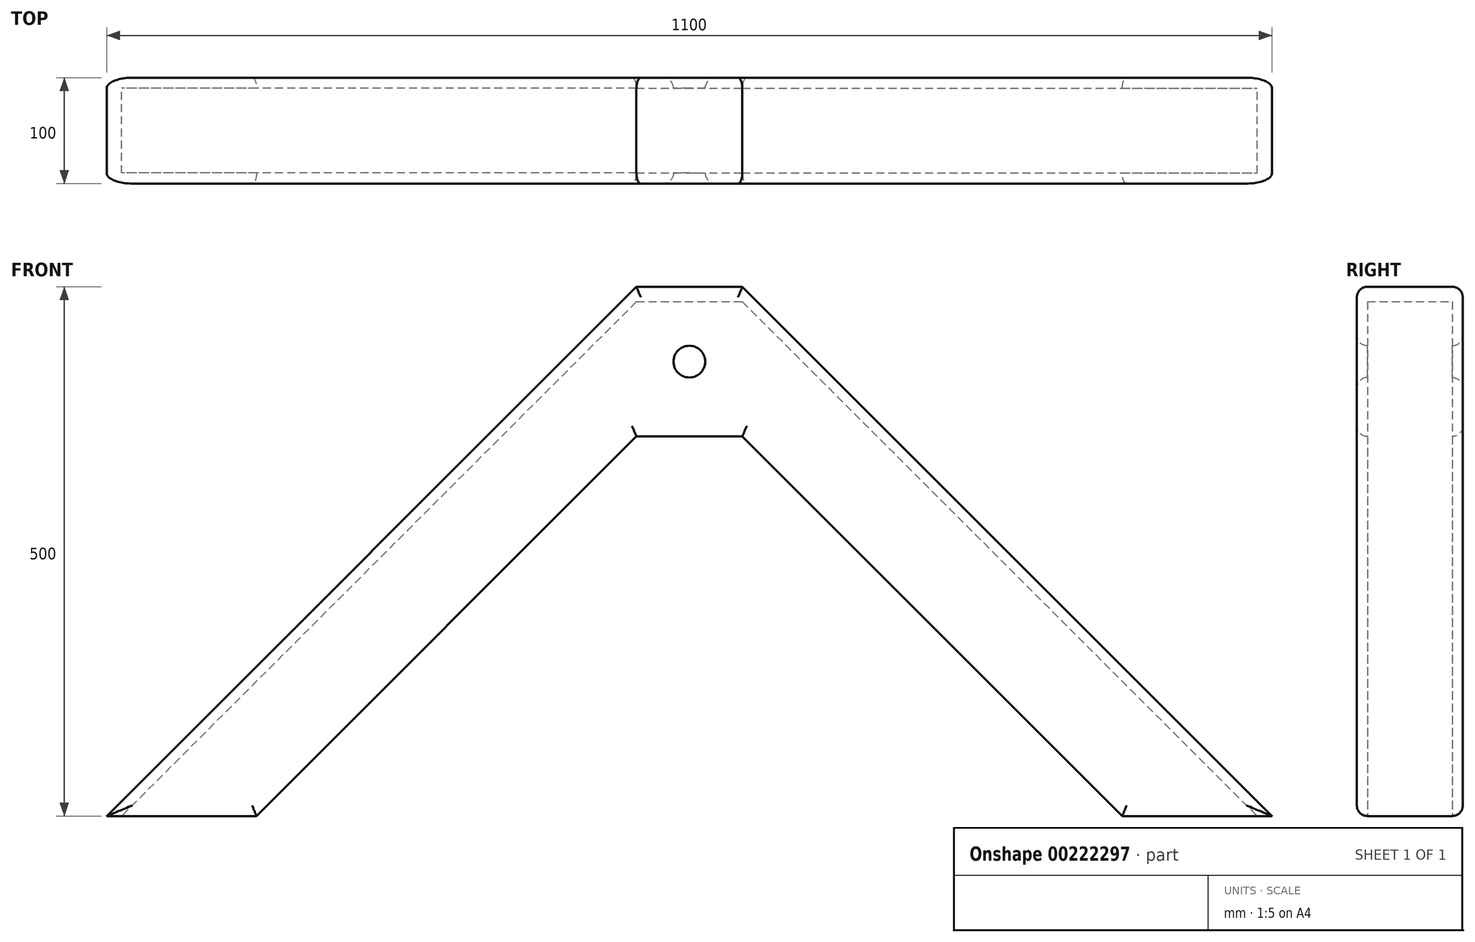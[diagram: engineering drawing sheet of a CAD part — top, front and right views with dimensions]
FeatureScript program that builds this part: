
annotation { "Feature Type Name" : "Feature", "Feature Type Description" : "" }
export const myFeature = defineFeature(function(context is Context, id is Id, definition is map)
    precondition{}
    {
        {
            var Q0;
            Q0=qCreatedBy(makeId("Front.planeOp"),FACE);
            var sketch = newSketch(context, id + "F0", { "sketchPlane" : qUnion([Q0])});
            skLineSegment(sketch, "E0", {"start": v(0, 500) * mm, "end": v(500, 0) * mm});
            skLineSegment(sketch, "E1.0", {"start": v(0, 358.58) * mm, "end": v(358.58, 0) * mm});
            skLineSegment(sketch, "E2", {"start": v(0, 500) * mm, "end": v(0, 0) * mm, "construction": true});
            skLineSegment(sketch, "E3", {"start": v(0, 0) * mm, "end": v(500, 0) * mm, "construction": true});
            skLineSegment(sketch, "E4", {"start": v(0, 485.86) * mm, "end": v(485.86, 0) * mm});
            skLineSegment(sketch, "E5", {"start": v(208.02, 291.98) * mm, "end": v(200.95, 284.9) * mm, "construction": true});
            skLineSegment(sketch, "E6", {"start": v(0, 358.58) * mm, "end": v(0, 500) * mm});
            skLineSegment(sketch, "E7", {"start": v(358.58, 0) * mm, "end": v(500, 0) * mm});
            skLineSegment(sketch, "E8.bottom", {"start": v(0, 500) * mm, "end": v(-50, 500) * mm});
            skLineSegment(sketch, "E8.top", {"start": v(0, 358.58) * mm, "end": v(-50, 358.58) * mm});
            skLineSegment(sketch, "E8.left", {"start": v(0, 500) * mm, "end": v(0, 358.58) * mm});
            skLineSegment(sketch, "E8.right", {"start": v(-50, 500) * mm, "end": v(-50, 358.58) * mm});
            skCircle(sketch, "E9", {"center": v(-50, 429.29) * mm, "radius": 15 * mm});
            skLineSegment(sketch, "E10", {"start": v(0, 485.86) * mm, "end": v(-50, 485.86) * mm});
            skSolve(sketch);
        }
        {
            var Q0;
            {var subQ0=sQuery(id+"F0.wireOp",EDGE,"E1.0");Q0=makeQuery(id+"F0.imprint","IMPRINT",FACE,{"disambiguationData":[TD([[makeQuery(id+"F0.imprint","IMPRINT",EDGE,{"derivedFrom":subQ0}),1.0]])]});}
            var Q1;
            {var subQ1=sQuery(id+"F0.wireOp",EDGE,"E8.top");Q1=makeQuery(id+"F0.imprint","IMPRINT",FACE,{"disambiguationData":[TD([[makeQuery(id+"F0.imprint","IMPRINT",EDGE,{"derivedFrom":subQ1}),-1.0]])]});}
            extrude(context, id + "F1", {"entities" : qUnion([Q0, Q1]), "depth" : 10 * mm, "offsetDistance" : 25 * mm});
        }
        {
            var Q0;
            {var subQ0=sQuery(id+"F0.wireOp",EDGE,"E0");Q0=makeQuery(id+"F0.imprint","IMPRINT",FACE,{"disambiguationData":[TD([[makeQuery(id+"F0.imprint","IMPRINT",EDGE,{"derivedFrom":subQ0}),-1.0]])]});}
            var Q1;
            {var subQ0=sQuery(id+"F0.wireOp",EDGE,"E8.bottom");Q1=makeQuery(id+"F0.imprint","IMPRINT",FACE,{"disambiguationData":[TD([[makeQuery(id+"F0.imprint","IMPRINT",EDGE,{"derivedFrom":subQ0}),1.0]])]});}
            extrude(context, id + "F2", {"entities" : qUnion([Q0, Q1]), "oppositeDirection" : true, "depth" : -50 * mm, "offsetDistance" : 25 * mm});
        }
        {
            var Q0;
            Q0=makeQuery(id+"F1.opExtrude","SWEPT_BODY",BODY,{"disambiguationData":[OSD([sQuery(id+"F0.wireOp",EDGE,"E1.0"),sQuery(id+"F0.wireOp",EDGE,"E4"),sQuery(id+"F0.wireOp",EDGE,"E6"),sQuery(id+"F0.wireOp",EDGE,"E7")])]});
            var Q1;
            Q1=makeQuery(id+"F2.opExtrude","SWEPT_BODY",BODY,{"disambiguationData":[OSD([sQuery(id+"F0.wireOp",EDGE,"E0"),sQuery(id+"F0.wireOp",EDGE,"E4"),sQuery(id+"F0.wireOp",EDGE,"E6"),sQuery(id+"F0.wireOp",EDGE,"E7")])]});
            var Q2;
            Q2=makeQuery(id+"F2.opExtrude","CAP_FACE",FACE,{"disambiguationData":[OSD([sQuery(id+"F0.wireOp",EDGE,"E0"),sQuery(id+"F0.wireOp",EDGE,"E4"),sQuery(id+"F0.wireOp",EDGE,"E6"),sQuery(id+"F0.wireOp",EDGE,"E7")])],"isStart":false});
            mirror(context, id + "F3", {"operationType" : NewBodyOperationType.ADD, "entities" : qUnion([Q0, Q1]), "mirrorPlane" : qUnion([Q2])});
        }
        {
            var Q0;
            Q0=makeQuery(id+"F1.opExtrude","SWEPT_BODY",BODY,{"disambiguationData":[OSD([sQuery(id+"F0.wireOp",EDGE,"E1.0"),sQuery(id+"F0.wireOp",EDGE,"E4"),sQuery(id+"F0.wireOp",EDGE,"E6"),sQuery(id+"F0.wireOp",EDGE,"E7")])]});
            var Q1;
            Q1=makeQuery(id+"F2.opExtrude","SWEPT_BODY",BODY,{"disambiguationData":[OSD([sQuery(id+"F0.wireOp",EDGE,"E0"),sQuery(id+"F0.wireOp",EDGE,"E4"),sQuery(id+"F0.wireOp",EDGE,"E6"),sQuery(id+"F0.wireOp",EDGE,"E7")])]});
            var Q2;
            {var subQ0=sQuery(id+"F0.wireOp",EDGE,"E8.right");var subQ1=makeQuery(id+"F2.opExtrude","SWEPT_FACE",FACE,{"disambiguationData":[OSD([subQ0])]});Q2=makeQuery(id+"F3.boolean.opBoolean","MERGE",FACE,{"derivedFrom":[subQ1,makeQuery(id+"F3.opPattern","COPY",FACE,{"derivedFrom":makeQuery(id+"F1.opExtrude","SWEPT_FACE",FACE,{"disambiguationData":[OSD([subQ0]),TDD([makeQuery(id+"F0.imprint","IMPRINT",EDGE,{"disambiguationData":[TD([[makeQuery(id+"F0.imprint","INTERSECT",VERTEX,{"derivedFrom":[subQ0,sQuery(id+"F0.wireOp",EDGE,"E10")]}),-1.0]])],"derivedFrom":subQ0})])]}),"instanceName":"1"}),makeQuery(id+"F3.opPattern","COPY",FACE,{"derivedFrom":subQ1,"instanceName":"1"})]});}
            mirror(context, id + "F4", {"entities" : qUnion([Q0, Q1]), "mirrorPlane" : qUnion([Q2])});
        }
        {
            var Q0;
            Q0=makeQuery(id+"F4.opPattern","COPY",BODY,{"derivedFrom":makeQuery(id+"F2.opExtrude","SWEPT_BODY",BODY,{"disambiguationData":[OSD([sQuery(id+"F0.wireOp",EDGE,"E0"),sQuery(id+"F0.wireOp",EDGE,"E4"),sQuery(id+"F0.wireOp",EDGE,"E6"),sQuery(id+"F0.wireOp",EDGE,"E7")])]}),"instanceName":"1"});
            var Q1;
            Q1=makeQuery(id+"F4.opPattern","COPY",BODY,{"derivedFrom":makeQuery(id+"F1.opExtrude","SWEPT_BODY",BODY,{"disambiguationData":[OSD([sQuery(id+"F0.wireOp",EDGE,"E1.0"),sQuery(id+"F0.wireOp",EDGE,"E4"),sQuery(id+"F0.wireOp",EDGE,"E6"),sQuery(id+"F0.wireOp",EDGE,"E7"),sQuery(id+"F0.wireOp",EDGE,"L2gpnRrP-EIs7-luCl-doRr-nX5twMeGKZvd")])]}),"instanceName":"1"});
            var Q2;
            Q2=makeQuery(id+"F2.opExtrude","SWEPT_BODY",BODY,{"disambiguationData":[OSD([sQuery(id+"F0.wireOp",EDGE,"E0"),sQuery(id+"F0.wireOp",EDGE,"E4"),sQuery(id+"F0.wireOp",EDGE,"E6"),sQuery(id+"F0.wireOp",EDGE,"E7")])]});
            var Q3;
            Q3=makeQuery(id+"F1.opExtrude","SWEPT_BODY",BODY,{"disambiguationData":[OSD([sQuery(id+"F0.wireOp",EDGE,"E1.0"),sQuery(id+"F0.wireOp",EDGE,"E4"),sQuery(id+"F0.wireOp",EDGE,"E6"),sQuery(id+"F0.wireOp",EDGE,"E7"),sQuery(id+"F0.wireOp",EDGE,"L2gpnRrP-EIs7-luCl-doRr-nX5twMeGKZvd")])]});
            booleanBodies(context, id + "F5", {"operationType" : BooleanOperationType.UNION, "tools" : qUnion([Q0, Q1, Q2, Q3])});
        }
        {
            var Q0;
            {var subQ0=sQuery(id+"F0.wireOp",EDGE,"E7");var subQ1=sQuery(id+"F0.wireOp",EDGE,"E6");var subQ2=sQuery(id+"F0.wireOp",EDGE,"E4");var subQ3=makeQuery(id+"F3.boolean.opBoolean","MERGE",FACE,{"derivedFrom":[makeQuery(id+"F3.opPattern","COPY",FACE,{"derivedFrom":makeQuery(id+"F1.opExtrude","CAP_FACE",FACE,{"disambiguationData":[OSD([sQuery(id+"F0.wireOp",EDGE,"E1.0"),subQ2,subQ1,subQ0,sQuery(id+"F0.wireOp",EDGE,"L2gpnRrP-EIs7-luCl-doRr-nX5twMeGKZvd")])],"isStart":true}),"instanceName":"1"}),makeQuery(id+"F3.opPattern","COPY",FACE,{"derivedFrom":makeQuery(id+"F2.opExtrude","CAP_FACE",FACE,{"disambiguationData":[OSD([sQuery(id+"F0.wireOp",EDGE,"E0"),subQ2,subQ1,subQ0])],"isStart":true}),"instanceName":"1"})]});Q0=makeQuery(id+"F5.opBoolean","MERGE",FACE,{"derivedFrom":[subQ3,makeQuery(id+"F4.opPattern","COPY",FACE,{"derivedFrom":subQ3,"instanceName":"1"})]});}
            var Q1;
            {var subQ0=sQuery(id+"F0.wireOp",EDGE,"E7");var subQ1=sQuery(id+"F0.wireOp",EDGE,"E6");var subQ2=sQuery(id+"F0.wireOp",EDGE,"E4");var subQ3=makeQuery(id+"F2.opExtrude","CAP_FACE",FACE,{"disambiguationData":[OSD([sQuery(id+"F0.wireOp",EDGE,"E0"),subQ2,subQ1,subQ0])],"isStart":true});var subQ4=makeQuery(id+"F1.opExtrude","CAP_FACE",FACE,{"disambiguationData":[OSD([sQuery(id+"F0.wireOp",EDGE,"E1.0"),subQ2,subQ1,subQ0,sQuery(id+"F0.wireOp",EDGE,"L2gpnRrP-EIs7-luCl-doRr-nX5twMeGKZvd")])],"isStart":true});Q1=makeQuery(id+"F5.opBoolean","MERGE",FACE,{"derivedFrom":[subQ4,subQ3,makeQuery(id+"F4.opPattern","COPY",FACE,{"derivedFrom":subQ4,"instanceName":"1"}),makeQuery(id+"F4.opPattern","COPY",FACE,{"derivedFrom":subQ3,"instanceName":"1"})]});}
            var Q2;
            {var subQ0=makeQuery(id+"F2.opExtrude","SWEPT_EDGE",EDGE,{"disambiguationData":[OSD([sQuery(id+"F0.wireOp",EDGE,"E0"),sQuery(id+"F0.wireOp",EDGE,"E6")])]});var subQ1=makeQuery(id+"F3.boolean.opBoolean","MERGE",EDGE,{"derivedFrom":[subQ0,makeQuery(id+"F3.opPattern","COPY",EDGE,{"derivedFrom":subQ0,"instanceName":"1"})]});Q2=makeQuery(id+"F5.opBoolean","MERGE",EDGE,{"derivedFrom":[subQ1,makeQuery(id+"F4.opPattern","COPY",EDGE,{"derivedFrom":subQ1,"instanceName":"1"})]});}
            fillet(context, id + "F6", {"entities" : qUnion([Q0, Q1, Q2]), "radius" : 10 * mm, "tangentPropagation" : true, "allowEdgeOverflow" : false});
        }
    });
